# Revit family: BRG-GRF-LVM- Vittoria Mezcladora Ducha 2 Funciones
name_source: partatom
category: Aparatos sanitarios
units: mm (PartAtom-declared; Revit-internal decimal feet)

## family parameters
Anfitrión = Muro
Compartido = No
Corte con vacíos al cargar = No
Cota de conector redondo = Diámetro de uso
Número OmniClass = 23.45.00.00
Punto de cálculo de habitación = No
Siempre vertical = Sí
Tipo de pieza = Normal
Título OmniClass = Sanitary, Laundry, and Cleaning Equipment

## types (1)
- Vittoria Mezcladora Ducha 2 Funciones
    Elevación por defecto = 0 m
    Fabricante = EDESA-PREMIUM
    Modelo = Vittoria Mezcladora Ducha 2 Funciones
    URL = https://edesa.com.ec
    _EDESA Consumo/capacidad de agua en L = 9.5 litros por minuto / 2.5 gpm en combinación con cualquiera de nuestras regaderas
    _EDESA_ Alto en cm = 18.5
    _EDESA_ Ancho en cm = 16
    _EDESA_ Certificación = Cumple con norma NTE - INEN 3123 basada en la norma ASME 112.18.1 - 2012.
    _EDESA_ Color = Cromo
    _EDESA_ Descripción = Grifería monomando de ducha 2 funciones para gua fría y caliente. Instalación empotrado en la pared
    _EDESA_ Manual de Instalacion = https://edesa.com.ec
    _EDESA_ Nombre = VITTORIA MEZCLADROA DE DUCHA 2 FUNCIONES
    _EDESA_ Productos necesarios para instalación = Regadera
    _EDESA_ Profundidad en cm = 9.4
    _EDESA_ Sku/código = SG0077633061CE
    _EDESA_ Tipo de instalación = Empotrado en la pared
    _EDESA_Categoría = Productos > Griferia > Ducha
    _EDESA_Conexión Hidraulica = Entrada de agua: Tubería ø 1/2"
    _EDESA_Garantia = De por vida para el cuerpo principal y acabado en cromo (306)
    _EDESA_Material = Latón
